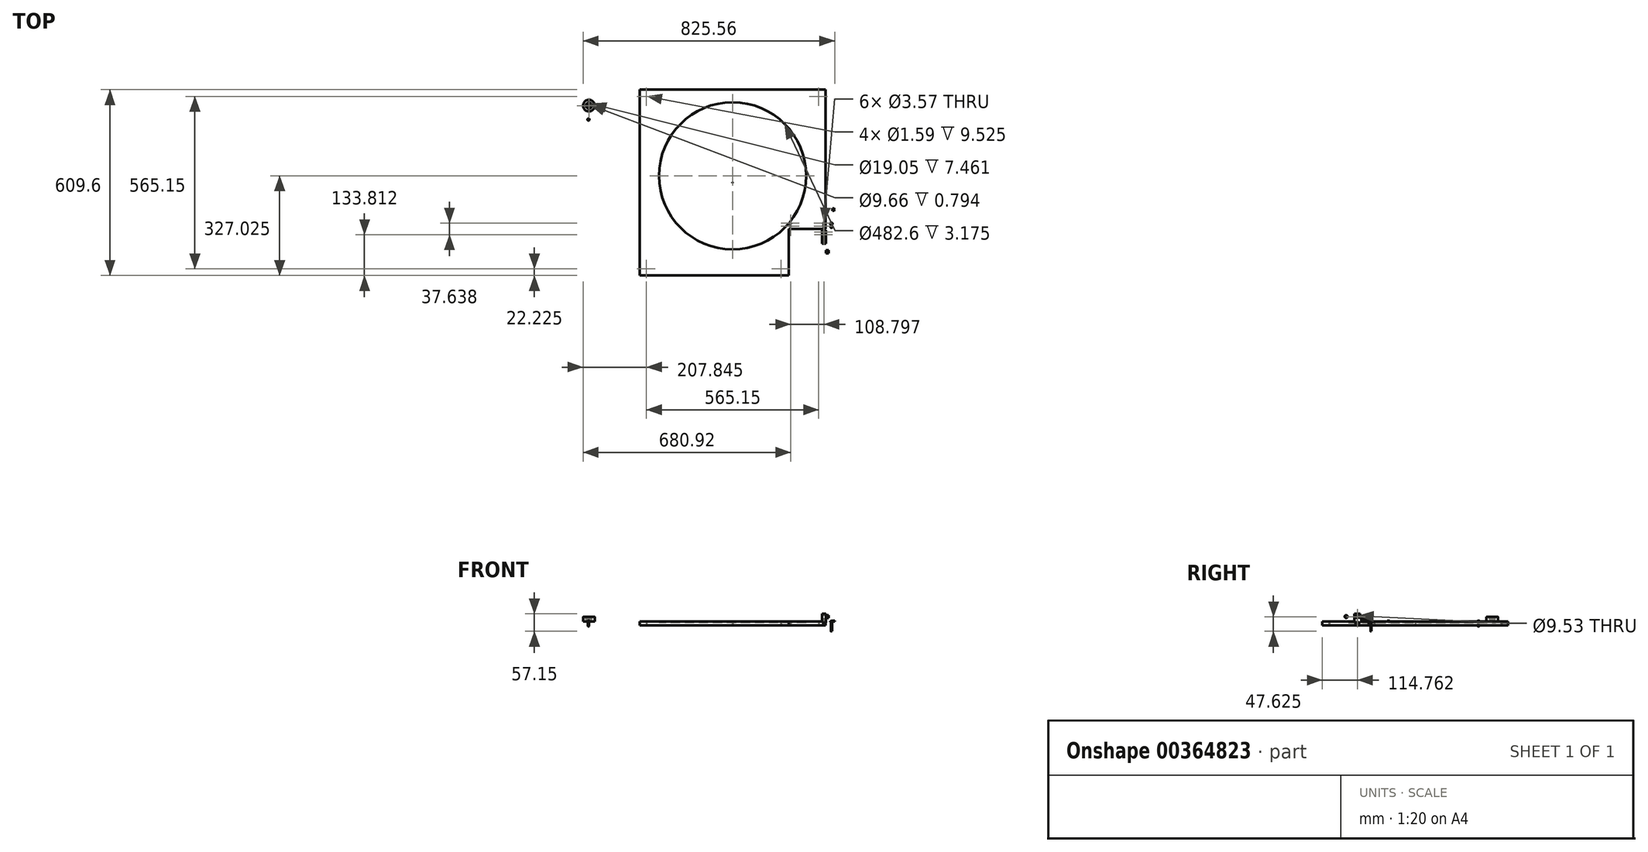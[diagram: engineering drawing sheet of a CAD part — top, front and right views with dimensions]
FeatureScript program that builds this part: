
annotation { "Feature Type Name" : "Feature", "Feature Type Description" : "" }
export const myFeature = defineFeature(function(context is Context, id is Id, definition is map)
    precondition{}
    {
        {
            var Q0;
            Q0=qCreatedBy(makeId("Top.planeOp"),FACE);
            var sketch = newSketch(context, id + "F0", { "sketchPlane" : qUnion([Q0])});
            skLineSegment(sketch, "E0.bottom", {"start": v(-304.8, 304.8) * mm, "end": v(304.8, 304.8) * mm});
            skLineSegment(sketch, "E0.top", {"start": v(-304.8, -304.8) * mm, "end": v(304.8, -304.8) * mm});
            skLineSegment(sketch, "E0.left", {"start": v(-304.8, 304.8) * mm, "end": v(-304.8, -304.8) * mm});
            skLineSegment(sketch, "E0.right", {"start": v(304.8, 304.8) * mm, "end": v(304.8, -304.8) * mm});
            skSolve(sketch);
        }
        {
            var Q0;
            Q0 = qSketchRegion(id + "F0", true);
            extrude(context, id + "F1", {"entities" : qUnion([Q0]), "oppositeDirection" : true, "depth" : 12.7 * mm});
        }
        {
            var Q0;
            Q0=makeQuery(id+"F1.opExtrude","CAP_FACE",FACE,{"disambiguationData":[OSD([sQuery(id+"F0.wireOp",EDGE,"E0.bottom"),sQuery(id+"F0.wireOp",EDGE,"E0.top"),sQuery(id+"F0.wireOp",EDGE,"E0.left"),sQuery(id+"F0.wireOp",EDGE,"E0.right")])],"isStart":true});
            var sketch = newSketch(context, id + "F2", { "sketchPlane" : qUnion([Q0])});
            skCircle(sketch, "E1", {"center": v(-471.37, 252.48) * mm, "radius": 19.05 * mm});
            skCircle(sketch, "E2", {"center": v(-471.37, 252.48) * mm, "radius": 3.97 * mm});
            skSolve(sketch);
        }
        {
            var Q0;
            Q0 = qSketchRegion(id + "F2", true);
            extrude(context, id + "F3", {"entities" : qUnion([Q0]), "depth" : 15.88 * mm});
        }
        {
            var Q0;
            Q0=makeQuery(id+"F3.opExtrude","CAP_FACE",FACE,{"disambiguationData":[OSD([sQuery(id+"F2.wireOp",EDGE,"E1"),sQuery(id+"F2.wireOp",EDGE,"E2")])],"isStart":false});
            var sketch = newSketch(context, id + "F4", { "sketchPlane" : qUnion([Q0])});
            skCircle(sketch, "E3", {"center": v(-471.37, 252.48) * mm, "radius": 9.53 * mm});
            skSolve(sketch);
        }
        {
            var Q0;
            Q0 = qSketchRegion(id + "F4", true);
            extrude(context, id + "F5", {"entities" : qUnion([Q0]), "operationType" : NewBodyOperationType.REMOVE, "oppositeDirection" : true, "depth" : 8.73 * mm});
        }
        {
            var Q0;
            Q0=makeQuery(id+"F3.opExtrude","CAP_FACE",FACE,{"disambiguationData":[OSD([sQuery(id+"F2.wireOp",EDGE,"E1"),sQuery(id+"F2.wireOp",EDGE,"E2")])],"isStart":false});
            fillet(context, id + "F6", {"entities" : qUnion([Q0]), "radius" : 1.27 * mm, "tangentPropagation" : true, "allowEdgeOverflow" : false});
        }
        {
            var Q0;
            Q0=makeQuery(id+"F5.boolean.opBoolean","COPY",FACE,{"derivedFrom":makeQuery(id+"F5.opExtrude","CAP_FACE",FACE,{"disambiguationData":[OSD([sQuery(id+"F4.wireOp",EDGE,"E3")])],"isStart":false})});
            var sketch = newSketch(context, id + "F7", { "sketchPlane" : qUnion([Q0])});
            skCircle(sketch, "E4", {"center": v(-471.37, 252.48) * mm, "radius": 8.88 * mm});
            skCircle(sketch, "E5", {"center": v(-471.37, 252.48) * mm, "radius": 4.83 * mm});
            skSolve(sketch);
        }
        {
            var Q0;
            Q0 = qSketchRegion(id + "F7", true);
            extrude(context, id + "F8", {"entities" : qUnion([Q0]), "operationType" : NewBodyOperationType.ADD, "depth" : 0.8 * mm});
        }
        {
            var Q0;
            Q0=makeQuery(id+"F1.opExtrude","CAP_FACE",FACE,{"disambiguationData":[OSD([sQuery(id+"F0.wireOp",EDGE,"E0.bottom"),sQuery(id+"F0.wireOp",EDGE,"E0.top"),sQuery(id+"F0.wireOp",EDGE,"E0.left"),sQuery(id+"F0.wireOp",EDGE,"E0.right")])],"isStart":false});
            var sketch = newSketch(context, id + "F9", { "sketchPlane" : qUnion([Q0])});
            skLineSegment(sketch, "E6.bottom", {"start": v(-282.58, 282.57) * mm, "end": v(282.58, 282.57) * mm, "construction": true});
            skLineSegment(sketch, "E6.top", {"start": v(-282.58, -282.58) * mm, "end": v(282.57, -282.58) * mm, "construction": true});
            skLineSegment(sketch, "E6.left", {"start": v(-282.58, 282.58) * mm, "end": v(-282.58, -282.58) * mm, "construction": true});
            skLineSegment(sketch, "E6.right", {"start": v(282.57, 282.58) * mm, "end": v(282.58, -282.58) * mm, "construction": true});
            skCircle(sketch, "E7", {"center": v(-282.58, 282.57) * mm, "radius": 0.8 * mm});
            skCircle(sketch, "E8", {"center": v(-282.58, -282.58) * mm, "radius": 0.8 * mm});
            skCircle(sketch, "E9", {"center": v(282.57, -282.58) * mm, "radius": 0.8 * mm});
            skCircle(sketch, "E10", {"center": v(0, 0) * mm, "radius": 0.8 * mm});
            skLineSegment(sketch, "E11.bottom", {"start": v(304.8, 304.8) * mm, "end": v(184.15, 304.8) * mm, "construction": true});
            skLineSegment(sketch, "E11.top", {"start": v(304.8, 152.4) * mm, "end": v(184.15, 152.4) * mm, "construction": true});
            skLineSegment(sketch, "E11.left", {"start": v(304.8, 304.8) * mm, "end": v(304.8, 152.4) * mm, "construction": true});
            skLineSegment(sketch, "E11.right", {"start": v(184.15, 304.8) * mm, "end": v(184.15, 152.4) * mm, "construction": true});
            skLineSegment(sketch, "E12", {"start": v(158.75, 296.57) * mm, "end": v(158.75, 241.24) * mm, "construction": true});
            skCircle(sketch, "E13", {"center": v(158.75, 282.58) * mm, "radius": 0.8 * mm});
            skLineSegment(sketch, "E14", {"start": v(244.47, 152.4) * mm, "end": v(244.47, 304.8) * mm, "construction": true});
            skCircle(sketch, "E15", {"center": v(244.47, 282.58) * mm, "radius": 0.8 * mm});
            skSolve(sketch);
        }
        {
            var Q0;
            Q0 = qSketchRegion(id + "F9", true);
            extrude(context, id + "F10", {"entities" : qUnion([Q0]), "operationType" : NewBodyOperationType.REMOVE, "oppositeDirection" : true, "depth" : 9.52 * mm});
        }
        {
            var Q0;
            Q0=makeQuery(id+"F1.opExtrude","CAP_FACE",FACE,{"disambiguationData":[OSD([sQuery(id+"F0.wireOp",EDGE,"E0.bottom"),sQuery(id+"F0.wireOp",EDGE,"E0.top"),sQuery(id+"F0.wireOp",EDGE,"E0.left"),sQuery(id+"F0.wireOp",EDGE,"E0.right")])],"isStart":true});
            var sketch = newSketch(context, id + "F11", { "sketchPlane" : qUnion([Q0])});
            skCircle(sketch, "E16", {"center": v(-472.53, 207.15) * mm, "radius": 3.43 * mm});
            skSolve(sketch);
        }
        {
            var Q0;
            Q0 = qSketchRegion(id + "F11", true);
            extrude(context, id + "F12", {"entities" : qUnion([Q0]), "depth" : 2.46 * mm});
        }
        {
            var Q0;
            Q0=makeQuery(id+"F12.opExtrude","CAP_FACE",FACE,{"disambiguationData":[OSD([sQuery(id+"F11.wireOp",EDGE,"E16")])],"isStart":false});
            var sketch = newSketch(context, id + "F13", { "sketchPlane" : qUnion([Q0])});
            skLineSegment(sketch, "E17.bottom", {"start": v(-474.74, 207.47) * mm, "end": v(-470.18, 207.47) * mm});
            skLineSegment(sketch, "E17.top", {"start": v(-474.74, 206.66) * mm, "end": v(-470.18, 206.66) * mm});
            skLineSegment(sketch, "E17.left", {"start": v(-474.74, 207.47) * mm, "end": v(-474.74, 206.66) * mm});
            skLineSegment(sketch, "E17.right", {"start": v(-470.18, 207.47) * mm, "end": v(-470.18, 206.66) * mm});
            skLineSegment(sketch, "E18.bottom", {"start": v(-473.07, 209.58) * mm, "end": v(-472.04, 209.58) * mm});
            skLineSegment(sketch, "E18.top", {"start": v(-473.07, 204.58) * mm, "end": v(-472.04, 204.58) * mm});
            skLineSegment(sketch, "E18.left", {"start": v(-473.07, 209.58) * mm, "end": v(-473.07, 204.58) * mm});
            skLineSegment(sketch, "E18.right", {"start": v(-472.04, 209.58) * mm, "end": v(-472.04, 204.58) * mm});
            skSolve(sketch);
        }
        {
            var Q0;
            Q0 = qSketchRegion(id + "F13", true);
            extrude(context, id + "F14", {"entities" : qUnion([Q0]), "operationType" : NewBodyOperationType.REMOVE, "oppositeDirection" : true, "depth" : 1.78 * mm});
        }
        {
            var Q0;
            Q0=makeQuery(id+"F12.opExtrude","CAP_EDGE",EDGE,{"disambiguationData":[OSD([sQuery(id+"F11.wireOp",EDGE,"E16")])],"isStart":false});
            fillet(context, id + "F15", {"entities" : qUnion([Q0]), "radius" : 1.02 * mm, "tangentPropagation" : true, "allowEdgeOverflow" : false});
        }
        {
            var Q0;
            Q0=makeQuery(id+"F12.opExtrude","CAP_FACE",FACE,{"disambiguationData":[OSD([sQuery(id+"F11.wireOp",EDGE,"E16")])],"isStart":true});
            var sketch = newSketch(context, id + "F16", { "sketchPlane" : qUnion([Q0])});
            skCircle(sketch, "E19", {"center": v(-472.53, -207.15) * mm, "radius": 1.75 * mm});
            skSolve(sketch);
        }
        {
            var Q0;
            Q0 = qSketchRegion(id + "F16", true);
            extrude(context, id + "F17", {"entities" : qUnion([Q0]), "operationType" : NewBodyOperationType.ADD, "depth" : 14.29 * mm});
        }
        {
            var Q0;
            Q0=makeQuery(id+"F17.opExtrude","CAP_FACE",FACE,{"disambiguationData":[OSD([sQuery(id+"F16.wireOp",EDGE,"E19")])],"isStart":false});
            var sketch = newSketch(context, id + "F18", { "sketchPlane" : qUnion([Q0])});
            skCircle(sketch, "E20", {"center": v(-472.53, -207.15) * mm, "radius": 1.71 * mm});
            skSolve(sketch);
        }
        {
            var Q0;
            Q0 = qSketchRegion(id + "F18", true);
            extrude(context, id + "F19", {"entities" : qUnion([Q0]), "operationType" : NewBodyOperationType.ADD, "depth" : 1.59 * mm, "hasDraft" : true, "draftAngle" : 30 * degree, "draftPullDirection" : true});
        }
        {
            var Q0;
            Q0=makeQuery(id+"F1.opExtrude","CAP_FACE",FACE,{"disambiguationData":[OSD([sQuery(id+"F0.wireOp",EDGE,"E0.bottom"),sQuery(id+"F0.wireOp",EDGE,"E0.top"),sQuery(id+"F0.wireOp",EDGE,"E0.left"),sQuery(id+"F0.wireOp",EDGE,"E0.right")])],"isStart":true});
            var sketch = newSketch(context, id + "F20", { "sketchPlane" : qUnion([Q0])});
            skCircle(sketch, "E21", {"center": v(0, 22.23) * mm, "radius": 241.3 * mm});
            skSolve(sketch);
        }
        {
            var Q0;
            Q0 = qSketchRegion(id + "F20", true);
            extrude(context, id + "F21", {"entities" : qUnion([Q0]), "operationType" : NewBodyOperationType.REMOVE, "oppositeDirection" : true, "depth" : 3.17 * mm});
        }
        {
            var Q0;
            Q0=makeQuery(id+"F1.opExtrude","CAP_FACE",FACE,{"disambiguationData":[OSD([sQuery(id+"F0.wireOp",EDGE,"E0.bottom"),sQuery(id+"F0.wireOp",EDGE,"E0.top"),sQuery(id+"F0.wireOp",EDGE,"E0.left"),sQuery(id+"F0.wireOp",EDGE,"E0.right")])],"isStart":true});
            var sketch = newSketch(context, id + "F22", { "sketchPlane" : qUnion([Q0])});
            skLineSegment(sketch, "E22.bottom", {"start": v(304.8, -304.8) * mm, "end": v(184.15, -304.8) * mm});
            skLineSegment(sketch, "E22.top", {"start": v(304.8, -152.4) * mm, "end": v(184.15, -152.4) * mm});
            skLineSegment(sketch, "E22.left", {"start": v(304.8, -304.8) * mm, "end": v(304.8, -152.4) * mm});
            skLineSegment(sketch, "E22.right", {"start": v(184.15, -304.8) * mm, "end": v(184.15, -152.4) * mm});
            skSolve(sketch);
        }
        {
            var Q0;
            Q0 = qSketchRegion(id + "F22", true);
            extrude(context, id + "F23", {"entities" : qUnion([Q0]), "operationType" : NewBodyOperationType.REMOVE, "oppositeDirection" : true, "depth" : 25.4 * mm});
        }
        {
            var Q0;
            Q0=makeQuery(id+"F1.opExtrude","CAP_FACE",FACE,{"disambiguationData":[OSD([sQuery(id+"F0.wireOp",EDGE,"E0.bottom"),sQuery(id+"F0.wireOp",EDGE,"E0.top"),sQuery(id+"F0.wireOp",EDGE,"E0.left"),sQuery(id+"F0.wireOp",EDGE,"E0.right")])],"isStart":true});
            var sketch = newSketch(context, id + "F24", { "sketchPlane" : qUnion([Q0])});
            skLineSegment(sketch, "E23.bottom", {"start": v(184.15, -152.4) * mm, "end": v(196.85, -152.4) * mm, "construction": true});
            skLineSegment(sketch, "E23.top", {"start": v(184.15, -127) * mm, "end": v(196.85, -127) * mm, "construction": true});
            skLineSegment(sketch, "E23.left", {"start": v(184.15, -152.4) * mm, "end": v(184.15, -127) * mm, "construction": true});
            skLineSegment(sketch, "E23.right", {"start": v(196.85, -152.4) * mm, "end": v(196.85, -127) * mm, "construction": true});
            skLineSegment(sketch, "E24.bottom", {"start": v(304.8, -152.4) * mm, "end": v(292.1, -152.4) * mm, "construction": true});
            skLineSegment(sketch, "E24.top", {"start": v(304.8, -127) * mm, "end": v(292.1, -127) * mm, "construction": true});
            skLineSegment(sketch, "E24.left", {"start": v(304.8, -152.4) * mm, "end": v(304.8, -127) * mm, "construction": true});
            skLineSegment(sketch, "E24.right", {"start": v(292.1, -152.4) * mm, "end": v(292.1, -127) * mm, "construction": true});
            skLineSegment(sketch, "E25", {"start": v(190.5, -127) * mm, "end": v(190.5, -152.4) * mm, "construction": true});
            skLineSegment(sketch, "E26", {"start": v(298.45, -127) * mm, "end": v(298.45, -152.4) * mm, "construction": true});
            skLineSegment(sketch, "E27", {"start": v(186.86, -133.35) * mm, "end": v(301.51, -133.35) * mm, "construction": true});
            skLineSegment(sketch, "E28", {"start": v(301.93, -142.87) * mm, "end": v(187.28, -142.87) * mm, "construction": true});
            skCircle(sketch, "E29", {"center": v(190.5, -133.35) * mm, "radius": 1.79 * mm});
            skCircle(sketch, "E30", {"center": v(190.5, -142.87) * mm, "radius": 1.79 * mm});
            skCircle(sketch, "E31", {"center": v(298.45, -133.35) * mm, "radius": 1.79 * mm});
            skCircle(sketch, "E32", {"center": v(298.45, -142.87) * mm, "radius": 1.79 * mm});
            skSolve(sketch);
        }
        {
            var Q0;
            Q0 = qSketchRegion(id + "F24", true);
            extrude(context, id + "F25", {"entities" : qUnion([Q0]), "operationType" : NewBodyOperationType.REMOVE, "oppositeDirection" : true, "depth" : 25.4 * mm});
        }
        {
            var Q0;
            Q0=makeQuery(id+"F21.boolean.opBoolean","COPY",FACE,{"derivedFrom":makeQuery(id+"F21.opExtrude","CAP_FACE",FACE,{"disambiguationData":[OSD([sQuery(id+"F20.wireOp",EDGE,"E21")])],"isStart":false})});
            var sketch = newSketch(context, id + "F26", { "sketchPlane" : qUnion([Q0])});
            skLineSegment(sketch, "E33.bottom", {"start": v(292.95, -155.11) * mm, "end": v(305.65, -155.11) * mm});
            skLineSegment(sketch, "E33.top", {"start": v(292.95, -199.56) * mm, "end": v(305.65, -199.56) * mm});
            skLineSegment(sketch, "E33.left", {"start": v(292.95, -155.11) * mm, "end": v(292.95, -199.56) * mm});
            skLineSegment(sketch, "E33.right", {"start": v(305.65, -155.11) * mm, "end": v(305.65, -199.56) * mm});
            skLineSegment(sketch, "E34", {"start": v(299.3, -155.11) * mm, "end": v(299.3, -199.56) * mm, "construction": true});
            skLineSegment(sketch, "E35", {"start": v(295.26, -161.46) * mm, "end": v(303.01, -161.46) * mm, "construction": true});
            skLineSegment(sketch, "E36", {"start": v(295.37, -170.99) * mm, "end": v(303.12, -170.99) * mm, "construction": true});
            skCircle(sketch, "E37", {"center": v(299.3, -161.46) * mm, "radius": 1.79 * mm});
            skCircle(sketch, "E38", {"center": v(299.3, -170.99) * mm, "radius": 1.79 * mm});
            skSolve(sketch);
        }
        {
            var Q0;
            Q0 = qSketchRegion(id + "F26", true);
            extrude(context, id + "F27", {"entities" : qUnion([Q0]), "depth" : 12.7 * mm});
        }
        {
            var Q0;
            Q0=makeQuery(id+"F27.opExtrude","CAP_FACE",FACE,{"disambiguationData":[OSD([sQuery(id+"F26.wireOp",EDGE,"E33.bottom"),sQuery(id+"F26.wireOp",EDGE,"E33.top"),sQuery(id+"F26.wireOp",EDGE,"E33.left"),sQuery(id+"F26.wireOp",EDGE,"E33.right"),sQuery(id+"F26.wireOp",EDGE,"E37"),sQuery(id+"F26.wireOp",EDGE,"E38")])],"isStart":false});
            var sketch = newSketch(context, id + "F28", { "sketchPlane" : qUnion([Q0])});
            skLineSegment(sketch, "E39.bottom", {"start": v(292.95, -199.56) * mm, "end": v(305.65, -199.56) * mm});
            skLineSegment(sketch, "E39.top", {"start": v(292.95, -180.51) * mm, "end": v(305.65, -180.51) * mm});
            skLineSegment(sketch, "E39.left", {"start": v(292.95, -199.56) * mm, "end": v(292.95, -180.51) * mm});
            skLineSegment(sketch, "E39.right", {"start": v(305.65, -199.56) * mm, "end": v(305.65, -180.51) * mm});
            skSolve(sketch);
        }
        {
            var Q0;
            Q0 = qSketchRegion(id + "F28", true);
            extrude(context, id + "F29", {"entities" : qUnion([Q0]), "operationType" : NewBodyOperationType.ADD, "depth" : 15.88 * mm});
        }
        {
            var Q0;
            Q0=makeQuery(id+"F29.boolean.opBoolean","MERGE",FACE,{"derivedFrom":[makeQuery(id+"F27.opExtrude","SWEPT_FACE",FACE,{"disambiguationData":[OSD([sQuery(id+"F26.wireOp",EDGE,"E33.right")])]}),makeQuery(id+"F29.opExtrude","SWEPT_FACE",FACE,{"disambiguationData":[OSD([sQuery(id+"F28.wireOp",EDGE,"E39.right")])]})]});
            var sketch = newSketch(context, id + "F30", { "sketchPlane" : qUnion([Q0])});
            skLineSegment(sketch, "E40", {"start": v(-190.04, 28.49) * mm, "end": v(-190.04, -5.19) * mm, "construction": true});
            skPoint(sketch, "E40.startSnap0", {"position": v(-190.04, 25.4) * mm});
            skLineSegment(sketch, "E41", {"start": v(-197.1, 15.88) * mm, "end": v(-184.13, 15.88) * mm, "construction": true});
            skCircle(sketch, "E42", {"center": v(-190.04, 15.88) * mm, "radius": 4.76 * mm});
            skSolve(sketch);
        }
        {
            var Q0;
            Q0 = qSketchRegion(id + "F30", true);
            extrude(context, id + "F31", {"entities" : qUnion([Q0]), "operationType" : NewBodyOperationType.REMOVE, "oppositeDirection" : true, "depth" : 25.4 * mm});
        }
        {
            var Q0;
            Q0=makeQuery(id+"F29.boolean.opBoolean","MERGE",FACE,{"derivedFrom":[makeQuery(id+"F27.opExtrude","SWEPT_FACE",FACE,{"disambiguationData":[OSD([sQuery(id+"F26.wireOp",EDGE,"E33.right")])]}),makeQuery(id+"F29.opExtrude","SWEPT_FACE",FACE,{"disambiguationData":[OSD([sQuery(id+"F28.wireOp",EDGE,"E39.right")])]})]});
            var sketch = newSketch(context, id + "F32", { "sketchPlane" : qUnion([Q0])});
            skCircle(sketch, "E43", {"center": v(-227, 16.54) * mm, "radius": 4.76 * mm});
            skCircle(sketch, "E44", {"center": v(-227, 16.54) * mm, "radius": 3.18 * mm});
            skSolve(sketch);
        }
        {
            var Q0;
            Q0=makeQuery(id+"F32.imprint","IMPRINT",FACE,{"disambiguationData":[TD([[makeQuery(id+"F32.imprint","IMPRINT",EDGE,{"derivedFrom":sQuery(id+"F32.wireOp",EDGE,"E43")}),1.0]])]});
            extrude(context, id + "F33", {"entities" : qUnion([Q0]), "depth" : 9.52 * mm});
        }
        {
            var Q0;
            Q0=makeQuery(id+"F1.opExtrude","CAP_FACE",FACE,{"disambiguationData":[OSD([sQuery(id+"F0.wireOp",EDGE,"E0.bottom"),sQuery(id+"F0.wireOp",EDGE,"E0.top"),sQuery(id+"F0.wireOp",EDGE,"E0.left"),sQuery(id+"F0.wireOp",EDGE,"E0.right")])],"isStart":true});
            var sketch = newSketch(context, id + "F34", { "sketchPlane" : qUnion([Q0])});
            skCircle(sketch, "E45", {"center": v(324.14, -145.29) * mm, "radius": 3.3 * mm});
            skSolve(sketch);
        }
        {
            var Q0;
            Q0 = qSketchRegion(id + "F34", true);
            extrude(context, id + "F35", {"entities" : qUnion([Q0]), "depth" : 2.62 * mm, "offsetDistance" : 25.4 * mm});
        }
        {
            var Q0;
            Q0=makeQuery(id+"F35.opExtrude","CAP_FACE",FACE,{"disambiguationData":[OSD([sQuery(id+"F34.wireOp",EDGE,"E45")])],"isStart":false});
            var sketch = newSketch(context, id + "F36", { "sketchPlane" : qUnion([Q0])});
            skLineSegment(sketch, "E46.bottom", {"start": v(321.86, -144.82) * mm, "end": v(326.24, -144.82) * mm});
            skLineSegment(sketch, "E46.top", {"start": v(321.86, -145.68) * mm, "end": v(326.24, -145.68) * mm});
            skLineSegment(sketch, "E46.left", {"start": v(321.86, -144.82) * mm, "end": v(321.86, -145.68) * mm});
            skLineSegment(sketch, "E46.right", {"start": v(326.24, -144.82) * mm, "end": v(326.24, -145.68) * mm});
            skLineSegment(sketch, "E47.bottom", {"start": v(323.68, -142.84) * mm, "end": v(324.6, -142.84) * mm});
            skLineSegment(sketch, "E47.top", {"start": v(323.68, -147.61) * mm, "end": v(324.6, -147.61) * mm});
            skLineSegment(sketch, "E47.left", {"start": v(323.68, -142.84) * mm, "end": v(323.68, -147.61) * mm});
            skLineSegment(sketch, "E47.right", {"start": v(324.6, -142.84) * mm, "end": v(324.6, -147.61) * mm});
            skSolve(sketch);
        }
        {
            var Q0;
            Q0 = qSketchRegion(id + "F36", true);
            extrude(context, id + "F37", {"entities" : qUnion([Q0]), "operationType" : NewBodyOperationType.REMOVE, "oppositeDirection" : true, "depth" : 2.3 * mm});
        }
        {
            var Q0;
            Q0=makeQuery(id+"F35.opExtrude","CAP_EDGE",EDGE,{"disambiguationData":[OSD([sQuery(id+"F34.wireOp",EDGE,"E45")])],"isStart":false});
            fillet(context, id + "F38", {"entities" : qUnion([Q0]), "radius" : 2.54 * mm, "tangentPropagation" : true, "allowEdgeOverflow" : false});
        }
        {
            var Q0;
            Q0=makeQuery(id+"F35.opExtrude","CAP_FACE",FACE,{"disambiguationData":[OSD([sQuery(id+"F34.wireOp",EDGE,"E45")])],"isStart":true});
            var sketch = newSketch(context, id + "F39", { "sketchPlane" : qUnion([Q0])});
            skCircle(sketch, "E48", {"center": v(324.14, 145.29) * mm, "radius": 1.75 * mm});
            skSolve(sketch);
        }
        {
            var Q0;
            Q0 = qSketchRegion(id + "F39", true);
            extrude(context, id + "F40", {"entities" : qUnion([Q0]), "operationType" : NewBodyOperationType.ADD, "depth" : 31.75 * mm, "offsetDistance" : 25.4 * mm});
        }
        {
            var Q0;
            Q0=makeQuery(id+"F1.opExtrude","CAP_FACE",FACE,{"disambiguationData":[OSD([sQuery(id+"F0.wireOp",EDGE,"E0.bottom"),sQuery(id+"F0.wireOp",EDGE,"E0.top"),sQuery(id+"F0.wireOp",EDGE,"E0.left"),sQuery(id+"F0.wireOp",EDGE,"E0.right")])],"isStart":true});
            var sketch = newSketch(context, id + "F41", { "sketchPlane" : qUnion([Q0])});
            skCircle(sketch, "E49", {"center": v(323.6, -134.85) * mm, "radius": 3.96 * mm});
            skCircle(sketch, "E50", {"center": v(323.6, -134.85) * mm, "radius": 1.98 * mm});
            skSolve(sketch);
        }
        {
            var Q0;
            Q0 = qSketchRegion(id + "F41", true);
            extrude(context, id + "F42", {"entities" : qUnion([Q0]), "oppositeDirection" : true, "depth" : 0.64 * mm});
        }
        {
            var Q0;
            Q0=makeQuery(id+"F1.opExtrude","CAP_FACE",FACE,{"disambiguationData":[OSD([sQuery(id+"F0.wireOp",EDGE,"E0.bottom"),sQuery(id+"F0.wireOp",EDGE,"E0.top"),sQuery(id+"F0.wireOp",EDGE,"E0.left"),sQuery(id+"F0.wireOp",EDGE,"E0.right")])],"isStart":true});
            var sketch = newSketch(context, id + "F43", { "sketchPlane" : qUnion([Q0])});
            skCircle(sketch, "E51.cCircle", {"center": v(330.56, -88) * mm, "radius": 3.97 * mm, "construction": true});
            skLineSegment(sketch, "E51.0", {"start": v(335.14, -88.05) * mm, "end": v(332.81, -92) * mm});
            skLineSegment(sketch, "E51.1", {"start": v(332.81, -92) * mm, "end": v(328.23, -91.95) * mm});
            skLineSegment(sketch, "E51.2", {"start": v(328.23, -91.95) * mm, "end": v(325.97, -87.96) * mm});
            skLineSegment(sketch, "E51.3", {"start": v(325.97, -87.96) * mm, "end": v(328.3, -84.01) * mm});
            skLineSegment(sketch, "E51.4", {"start": v(328.3, -84.01) * mm, "end": v(332.88, -84.06) * mm});
            skLineSegment(sketch, "E51.5", {"start": v(332.88, -84.06) * mm, "end": v(335.14, -88.05) * mm});
            skPoint(sketch, "E51.0.midPoint", {"position": v(333.98, -90.02) * mm});
            skCircle(sketch, "E52", {"center": v(330.56, -88) * mm, "radius": 1.98 * mm});
            skSolve(sketch);
        }
        {
            var Q0;
            Q0 = qSketchRegion(id + "F43", true);
            extrude(context, id + "F44", {"entities" : qUnion([Q0]), "depth" : 2.78 * mm});
        }
        {
            var Q0;
            Q0=makeQuery(id+"F27.opExtrude","CAP_FACE",FACE,{"disambiguationData":[OSD([sQuery(id+"F26.wireOp",EDGE,"E33.bottom"),sQuery(id+"F26.wireOp",EDGE,"E33.top"),sQuery(id+"F26.wireOp",EDGE,"E33.left"),sQuery(id+"F26.wireOp",EDGE,"E33.right"),sQuery(id+"F26.wireOp",EDGE,"E37"),sQuery(id+"F26.wireOp",EDGE,"E38")])],"isStart":true});
            var sketch = newSketch(context, id + "F45", { "sketchPlane" : qUnion([Q0])});
            skLineSegment(sketch, "E53", {"start": v(299.3, 202.21) * mm, "end": v(299.3, 153.67) * mm, "construction": true});
            skPoint(sketch, "E53.startSnap0", {"position": v(299.3, 199.56) * mm});
            skPoint(sketch, "E53.endSnap0", {"position": v(299.3, 155.11) * mm});
            skCircle(sketch, "E54", {"center": v(299.3, 190.04) * mm, "radius": 3.18 * mm});
            skCircle(sketch, "E55", {"center": v(299.3, 190.04) * mm, "radius": 5.56 * mm, "construction": true});
            skSolve(sketch);
        }
        {
            var Q0;
            Q0 = qSketchRegion(id + "F45", true);
            extrude(context, id + "F46", {"entities" : qUnion([Q0]), "operationType" : NewBodyOperationType.REMOVE, "oppositeDirection" : true, "depth" : 4.76 * mm, "offsetDistance" : 25.4 * mm});
        }
        {
            var Q0;
            Q0=makeQuery(id+"F27.opExtrude","CAP_FACE",FACE,{"disambiguationData":[OSD([sQuery(id+"F26.wireOp",EDGE,"E33.bottom"),sQuery(id+"F26.wireOp",EDGE,"E33.top"),sQuery(id+"F26.wireOp",EDGE,"E33.left"),sQuery(id+"F26.wireOp",EDGE,"E33.right"),sQuery(id+"F26.wireOp",EDGE,"E37"),sQuery(id+"F26.wireOp",EDGE,"E38")])],"isStart":true});
            var sketch = newSketch(context, id + "F47", { "sketchPlane" : qUnion([Q0])});
            skLineSegment(sketch, "E56.bottom", {"start": v(305.65, 155.11) * mm, "end": v(292.95, 155.11) * mm});
            skLineSegment(sketch, "E56.top", {"start": v(305.65, 180.51) * mm, "end": v(292.95, 180.51) * mm});
            skLineSegment(sketch, "E56.left", {"start": v(305.65, 155.11) * mm, "end": v(305.65, 180.51) * mm});
            skLineSegment(sketch, "E56.right", {"start": v(292.95, 155.11) * mm, "end": v(292.95, 180.51) * mm});
            skSolve(sketch);
        }
        {
            var Q0;
            Q0 = qSketchRegion(id + "F47", true);
            extrude(context, id + "F48", {"entities" : qUnion([Q0]), "operationType" : NewBodyOperationType.REMOVE, "oppositeDirection" : true, "depth" : 3.17 * mm, "offsetDistance" : 25.4 * mm});
        }
    });
